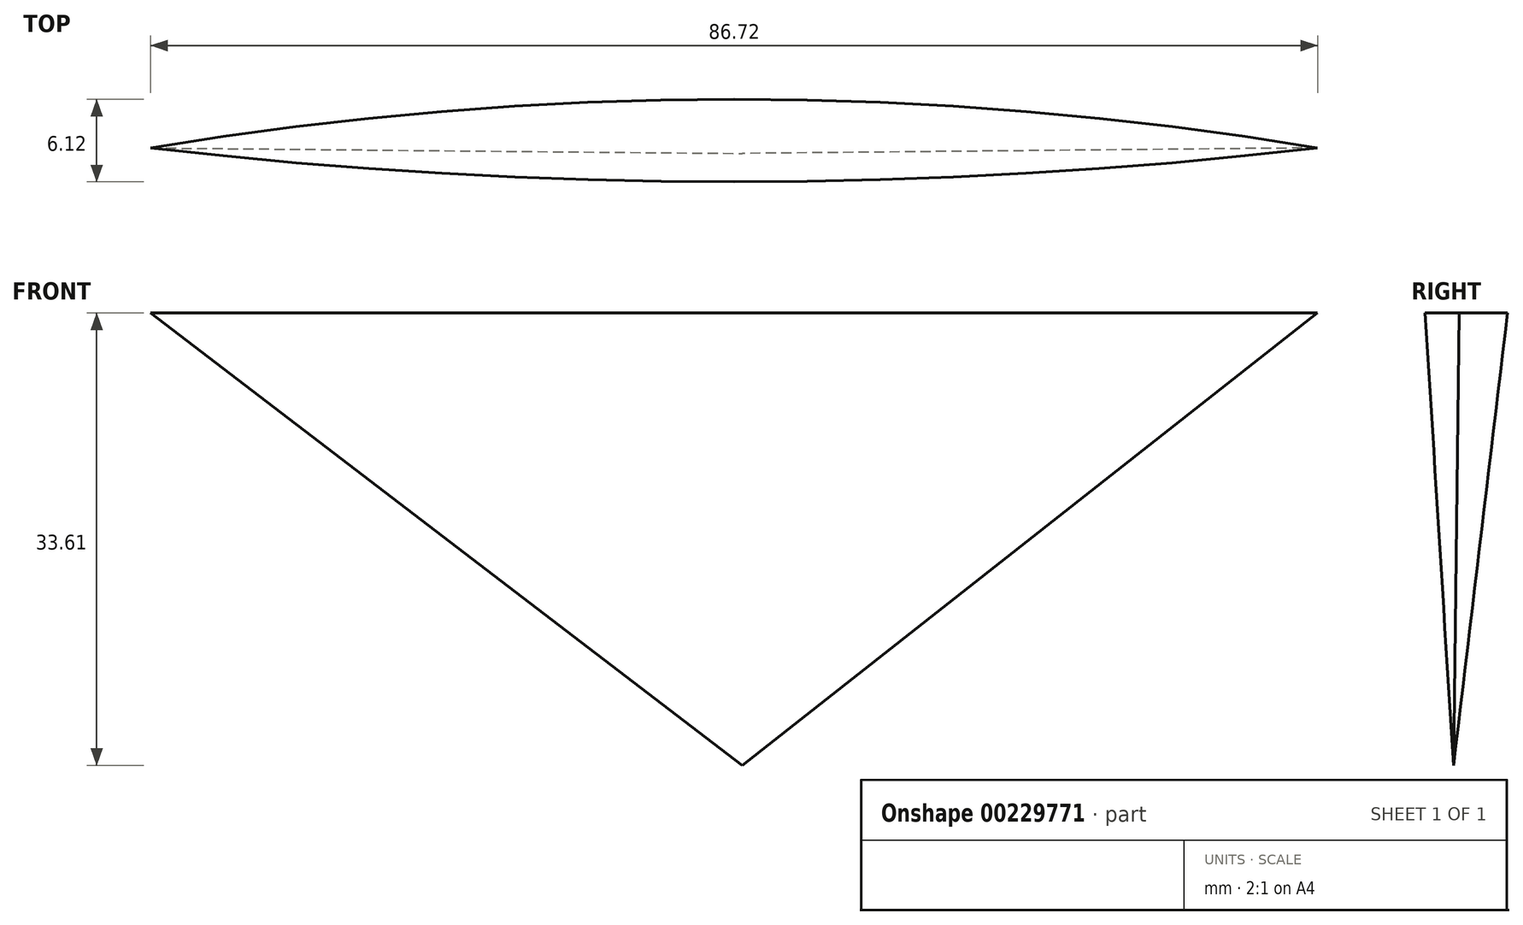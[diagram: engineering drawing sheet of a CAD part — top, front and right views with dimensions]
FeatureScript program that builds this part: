
annotation { "Feature Type Name" : "Feature", "Feature Type Description" : "" }
export const myFeature = defineFeature(function(context is Context, id is Id, definition is map)
    precondition{}
    {
        {
            var Q0;
            Q0=qCreatedBy(makeId("Top.planeOp"),FACE);
            var sketch = newSketch(context, id + "F0", { "sketchPlane" : qUnion([Q0])});
            skArc(sketch, "E0", {"start": v(-43.98, 0.41) * mm, "mid": v(-0.62, -2.1) * mm, "end": v(42.74, 0.41) * mm});
            skArc(sketch, "E1", {"start": v(42.74, 0.41) * mm, "mid": v(-0.62, 4.02) * mm, "end": v(-43.98, 0.41) * mm});
            skSolve(sketch);
        }
        {
            var Q0;
            Q0=qCreatedBy(makeId("Front.planeOp"),FACE);
            var sketch = newSketch(context, id + "F1", { "sketchPlane" : qUnion([Q0])});
            skLineSegment(sketch, "E2", {"start": v(0, 34.85) * mm, "end": v(0, -33.6) * mm});
            skSolve(sketch);
        }
        {
            var Q0;
            Q0=makeQuery(id+"F0.imprint","IMPRINT",FACE,{"disambiguationData":[TD([[makeQuery(id+"F0.imprint","IMPRINT",EDGE,{"derivedFrom":sQuery(id+"F0.wireOp",EDGE,"E0")}),1.0]])]});
            var Q1;
            Q1=sQuery(id+"F1.wireOp",VERTEX,"E2.end");
            loft(context, id + "F2", {"sheetProfilesArray" : [{ "sheetProfileEntities" : qUnion([Q0]) }, { "sheetProfileEntities" : qUnion([Q1]) }]});
        }
    });
